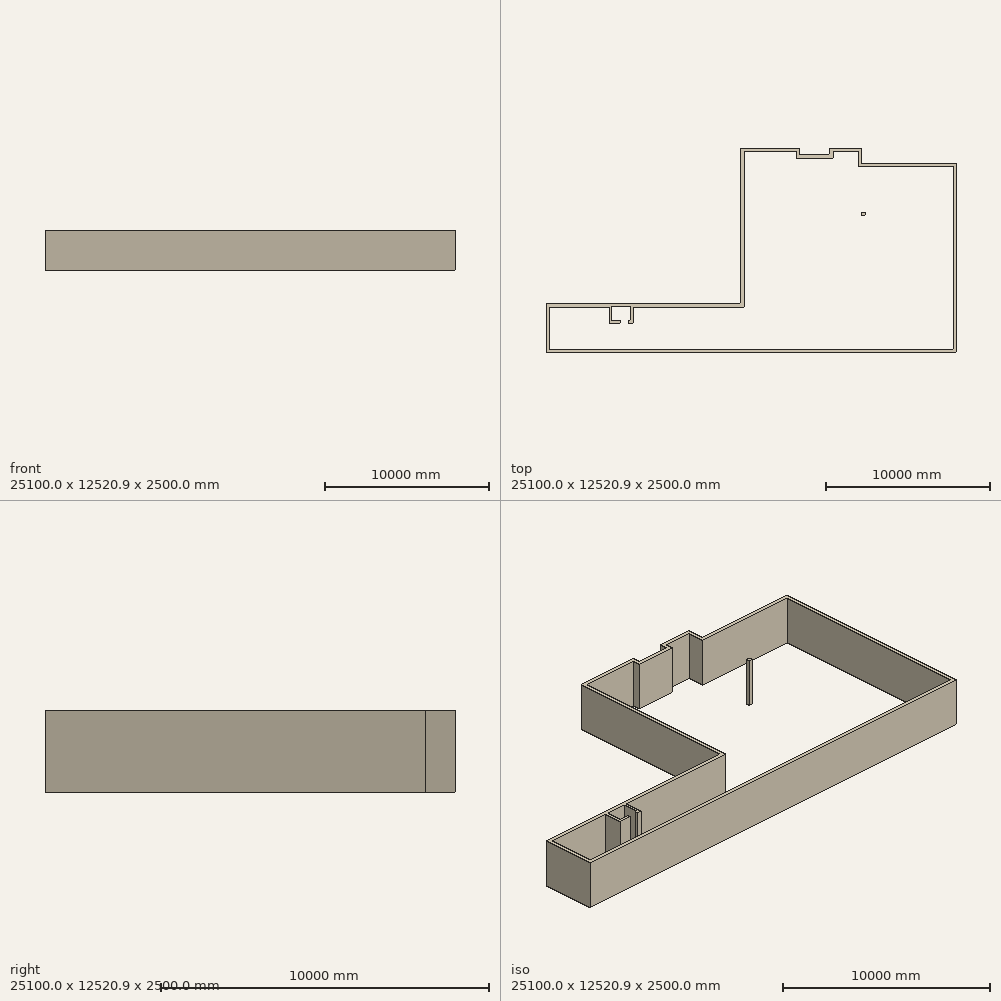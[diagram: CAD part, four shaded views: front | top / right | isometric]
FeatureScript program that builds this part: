
annotation { "Feature Type Name" : "Feature", "Feature Type Description" : "" }
export const myFeature = defineFeature(function(context is Context, id is Id, definition is map)
    precondition{}
    {
        {
            var Q0;
            Q0=qCreatedBy(makeId("Top.planeOp"),FACE);
            var sketch = newSketch(context, id + "F0", { "sketchPlane" : qUnion([Q0])});
            skLineSegment(sketch, "E0", {"start": v(-4493, 1183.43) * mm, "end": v(-4493, -1416.57) * mm});
            skLineSegment(sketch, "E1", {"start": v(612, 1183.43) * mm, "end": v(7407, 1183.43) * mm});
            skLineSegment(sketch, "E2", {"start": v(7407, 10704.28) * mm, "end": v(7407, 1183.43) * mm});
            skLineSegment(sketch, "E3", {"start": v(7407, 10704.28) * mm, "end": v(10595.94, 10704.28) * mm});
            skLineSegment(sketch, "E4", {"start": v(10595.94, 10704.28) * mm, "end": v(10595.94, 10300.26) * mm});
            skLineSegment(sketch, "E5", {"start": v(10595.94, 10300.26) * mm, "end": v(12855.25, 10300.26) * mm});
            skLineSegment(sketch, "E6", {"start": v(12855.25, 10300.26) * mm, "end": v(12855.25, 10704.28) * mm});
            skLineSegment(sketch, "E7", {"start": v(12855.25, 10704.28) * mm, "end": v(14407, 10704.28) * mm});
            skLineSegment(sketch, "E8", {"start": v(14407, 10704.28) * mm, "end": v(14407, 9783.43) * mm});
            skLineSegment(sketch, "E9", {"start": v(14407, 9783.43) * mm, "end": v(20207, 9783.43) * mm});
            skLineSegment(sketch, "E10", {"start": v(20207, 9783.43) * mm, "end": v(20207, -1416.57) * mm});
            skLineSegment(sketch, "E11", {"start": v(20207, -1416.57) * mm, "end": v(-4493, -1416.57) * mm});
            skLineSegment(sketch, "E12", {"start": v(-4493, 189.82) * mm, "end": v(-4493, 1183.43) * mm, "construction": true});
            skLineSegment(sketch, "E13", {"start": v(-4493, 189.82) * mm, "end": v(607, 189.82) * mm, "construction": true});
            skLineSegment(sketch, "E14", {"start": v(607, 189.82) * mm, "end": v(7407, 189.82) * mm, "construction": true});
            skLineSegment(sketch, "E15.bottom", {"start": v(14607, 6983.43) * mm, "end": v(14816.3, 6983.43) * mm});
            skLineSegment(sketch, "E15.top", {"start": v(14607, 6774.13) * mm, "end": v(14816.3, 6774.13) * mm});
            skLineSegment(sketch, "E15.left", {"start": v(14816.3, 6983.43) * mm, "end": v(14816.3, 6774.13) * mm});
            skLineSegment(sketch, "E15.right", {"start": v(14607, 6983.43) * mm, "end": v(14607, 6774.13) * mm});
            skLineSegment(sketch, "E16", {"start": v(14407, 9783.43) * mm, "end": v(13771.9, 9783.43) * mm, "construction": true});
            skLineSegment(sketch, "E17", {"start": v(13771.9, 9783.43) * mm, "end": v(13771.9, 6983.43) * mm, "construction": true});
            skLineSegment(sketch, "E18", {"start": v(13771.9, 6983.43) * mm, "end": v(14816.3, 6983.43) * mm, "construction": true});
            skLineSegment(sketch, "E19", {"start": v(7407, 1183.43) * mm, "end": v(7407, -4110.55) * mm, "construction": true});
            skLineSegment(sketch, "E20", {"start": v(7407, -4110.55) * mm, "end": v(20207, -4110.55) * mm});
            skLineSegment(sketch, "E21", {"start": v(20207, -4110.55) * mm, "end": v(20207, -1416.57) * mm, "construction": true});
            skLineSegment(sketch, "E22", {"start": v(7407, 10704.28) * mm, "end": v(7407, 12253.73) * mm, "construction": true});
            skLineSegment(sketch, "E23", {"start": v(7407, 12253.73) * mm, "end": v(14407, 12253.73) * mm, "construction": true});
            skLineSegment(sketch, "E24", {"start": v(14407, 12253.73) * mm, "end": v(14407, 10704.28) * mm, "construction": true});
            skLineSegment(sketch, "E25", {"start": v(14607, 6774.13) * mm, "end": v(7407, 6774.13) * mm, "construction": true});
            skLineSegment(sketch, "E26.0", {"start": v(-4693, 1383.43) * mm, "end": v(-4693, -1616.57) * mm});
            skLineSegment(sketch, "E26.1", {"start": v(20407, -1616.57) * mm, "end": v(-4693, -1616.57) * mm});
            skLineSegment(sketch, "E26.2", {"start": v(20407, 9983.43) * mm, "end": v(20407, -1616.57) * mm});
            skLineSegment(sketch, "E26.3", {"start": v(14607, 9983.43) * mm, "end": v(20407, 9983.43) * mm});
            skLineSegment(sketch, "E26.4", {"start": v(14607, 10904.28) * mm, "end": v(14607, 9983.43) * mm});
            skLineSegment(sketch, "E26.5", {"start": v(-4693, 1383.43) * mm, "end": v(7207, 1383.43) * mm});
            skLineSegment(sketch, "E26.6", {"start": v(12655.25, 10904.28) * mm, "end": v(14607, 10904.28) * mm});
            skLineSegment(sketch, "E26.7", {"start": v(12655.25, 10500.26) * mm, "end": v(12655.25, 10904.28) * mm});
            skLineSegment(sketch, "E26.8", {"start": v(10795.94, 10500.26) * mm, "end": v(12655.25, 10500.26) * mm});
            skLineSegment(sketch, "E26.9", {"start": v(10795.94, 10904.28) * mm, "end": v(10795.94, 10500.26) * mm});
            skLineSegment(sketch, "E26.10", {"start": v(7207, 10904.28) * mm, "end": v(10795.94, 10904.28) * mm});
            skLineSegment(sketch, "E26.11", {"start": v(7207, 10904.28) * mm, "end": v(7207, 1383.43) * mm});
            skLineSegment(sketch, "E27", {"start": v(607, 189.82) * mm, "end": v(607, 1178.43) * mm});
            skLineSegment(sketch, "E28", {"start": v(-160.62, 189.82) * mm, "end": v(-833.18, 189.82) * mm});
            skLineSegment(sketch, "E29", {"start": v(-833.18, 189.82) * mm, "end": v(-833.18, 1183.43) * mm});
            skArc(sketch, "E30.filletArc", {"start": v(612, 1183.43) * mm, "mid": v(608.47, 1181.97) * mm, "end": v(607, 1178.43) * mm});
            skLineSegment(sketch, "E31", {"start": v(-833.18, 1183.43) * mm, "end": v(-4493, 1183.43) * mm});
            skLineSegment(sketch, "E32.0", {"start": v(-683.18, 339.82) * mm, "end": v(-683.18, 1185.93) * mm});
            skLineSegment(sketch, "E32.1", {"start": v(-160.62, 339.82) * mm, "end": v(-683.18, 339.82) * mm});
            skLineSegment(sketch, "E32.2", {"start": v(457, 339.82) * mm, "end": v(457, 1185.93) * mm});
            skLineSegment(sketch, "E33", {"start": v(-155.62, 334.82) * mm, "end": v(-155.62, 194.82) * mm});
            skLineSegment(sketch, "E34", {"start": v(341.97, 334.82) * mm, "end": v(341.97, 194.82) * mm});
            skLineSegment(sketch, "E35", {"start": v(-683.18, 1185.93) * mm, "end": v(457, 1185.93) * mm});
            skArc(sketch, "E36.filletArc", {"start": v(-155.62, 334.82) * mm, "mid": v(-157.09, 338.36) * mm, "end": v(-160.62, 339.82) * mm});
            skArc(sketch, "E37.filletArc", {"start": v(-160.62, 189.82) * mm, "mid": v(-157.09, 191.29) * mm, "end": v(-155.62, 194.82) * mm});
            skLineSegment(sketch, "E38", {"start": v(457, 339.82) * mm, "end": v(346.97, 339.82) * mm});
            skLineSegment(sketch, "E39", {"start": v(607, 189.82) * mm, "end": v(346.97, 189.82) * mm});
            skArc(sketch, "E40.filletArc", {"start": v(341.97, 194.82) * mm, "mid": v(343.44, 191.29) * mm, "end": v(346.97, 189.82) * mm});
            skArc(sketch, "E41.filletArc", {"start": v(346.97, 339.82) * mm, "mid": v(343.44, 338.36) * mm, "end": v(341.97, 334.82) * mm});
            skSolve(sketch);
        }
        {
            var Q0;
            Q0 = qSketchRegion(id + "F0", true);
            var Q1;
            Q1=makeQuery(id+"F0.imprint","IMPRINT",FACE,{"disambiguationData":[TD([[makeQuery(id+"F0.imprint","IMPRINT",EDGE,{"derivedFrom":sQuery(id+"F0.wireOp",EDGE,"E15.bottom")}),-1.0]])]});
            extrude(context, id + "F1", {"entities" : qUnion([Q0, Q1]), "depth" : 2500 * mm});
        }
    });
